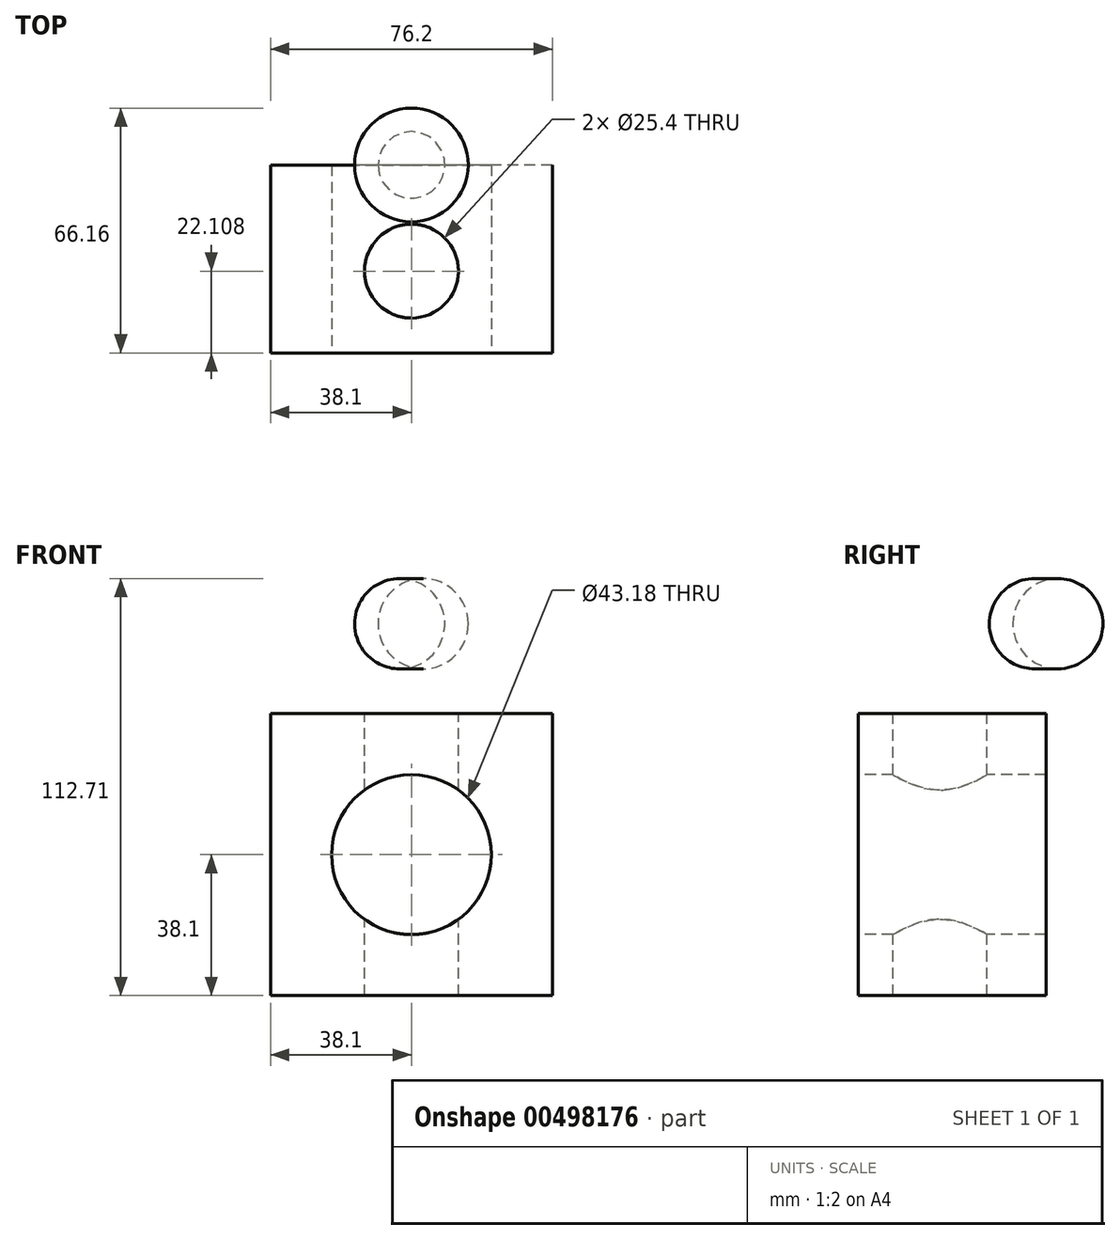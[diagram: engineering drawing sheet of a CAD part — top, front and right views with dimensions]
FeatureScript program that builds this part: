
annotation { "Feature Type Name" : "Feature", "Feature Type Description" : "" }
export const myFeature = defineFeature(function(context is Context, id is Id, definition is map)
    precondition{}
    {
        {
            var Q0;
            Q0=qCreatedBy(makeId("Front.planeOp"),FACE);
            var sketch = newSketch(context, id + "F0", { "sketchPlane" : qUnion([Q0])});
            skLineSegment(sketch, "E0", {"start": v(0, 0) * mm, "end": v(0, -36.26) * mm, "construction": true});
            skSolve(sketch);
        }
        {
            var Q0;
            Q0=qCreatedBy(makeId("Front.planeOp"),FACE);
            var sketch = newSketch(context, id + "F1", { "sketchPlane" : qUnion([Q0])});
            skLineSegment(sketch, "E1.bottom", {"start": v(38.1, 38.1) * mm, "end": v(-38.1, 38.1) * mm});
            skLineSegment(sketch, "E1.top", {"start": v(38.1, -38.1) * mm, "end": v(-38.1, -38.1) * mm});
            skLineSegment(sketch, "E1.left", {"start": v(38.1, 38.1) * mm, "end": v(38.1, -38.1) * mm});
            skLineSegment(sketch, "E1.right", {"start": v(-38.1, 38.1) * mm, "end": v(-38.1, -38.1) * mm});
            skPoint(sketch, "E1.middle", {"position": v(0, 0) * mm});
            skSolve(sketch);
        }
        {
            var Q0;
            Q0 = qSketchRegion(id + "F1", true);
            extrude(context, id + "F2", {"entities" : qUnion([Q0]), "depth" : 50.8 * mm, "offsetDistance" : 25.4 * mm});
        }
        {
            var Q0;
            Q0=makeQuery(id+"F2.opExtrude","SWEPT_FACE",FACE,{"disambiguationData":[OSD([sQuery(id+"F1.wireOp",EDGE,"E1.bottom")])]});
            var sketch = newSketch(context, id + "F3", { "sketchPlane" : qUnion([Q0])});
            skCircle(sketch, "E2", {"center": v(0, -28.7) * mm, "radius": 12.7 * mm});
            skSolve(sketch);
        }
        {
            var Q0;
            Q0 = qSketchRegion(id + "F3", true);
            extrude(context, id + "F4", {"entities" : qUnion([Q0]), "operationType" : NewBodyOperationType.REMOVE, "endBound" : BoundingType.THROUGH_ALL, "oppositeDirection" : true, "depth" : 25.4 * mm, "offsetDistance" : 25.4 * mm});
        }
        {
            var Q0;
            Q0=qCreatedBy(makeId("Front.planeOp"),FACE);
            var sketch = newSketch(context, id + "F5", { "sketchPlane" : qUnion([Q0])});
            skLineSegment(sketch, "E3", {"start": v(0, 50.64) * mm, "end": v(0, 74.2) * mm, "construction": true});
            skArc(sketch, "E4", {"start": v(0, 50.64) * mm, "mid": v(9.03, 62.42) * mm, "end": v(0, 74.2) * mm});
            skLineSegment(sketch, "E5", {"start": v(0, 74.2) * mm, "end": v(0, 50.64) * mm});
            skSolve(sketch);
        }
        {
            var Q0;
            Q0=makeQuery(id+"F5.imprint","IMPRINT",FACE,{"disambiguationData":[TD([[makeQuery(id+"F5.imprint","IMPRINT",EDGE,{"derivedFrom":sQuery(id+"F5.wireOp",EDGE,"E4")}),1.0]])]});
            var Q1;
            Q1=sQuery(id+"F5.wireOp",EDGE,"E5");
            revolve(context, id + "F6", {"entities" : qUnion([Q0]), "axis" : qUnion([Q1]), "revolveType" : RevolveType.FULL});
        }
        {
            var Q0;
            Q0=makeQuery(id+"F2.opExtrude","CAP_FACE",FACE,{"disambiguationData":[OSD([sQuery(id+"F1.wireOp",EDGE,"E1.bottom"),sQuery(id+"F1.wireOp",EDGE,"E1.top"),sQuery(id+"F1.wireOp",EDGE,"E1.left"),sQuery(id+"F1.wireOp",EDGE,"E1.right")])],"isStart":false});
            var sketch = newSketch(context, id + "F7", { "sketchPlane" : qUnion([Q0])});
            skCircle(sketch, "E6", {"center": v(0, 0) * mm, "radius": 21.59 * mm});
            skSolve(sketch);
        }
        {
            var Q0;
            Q0 = qSketchRegion(id + "F7", true);
            extrude(context, id + "F8", {"entities" : qUnion([Q0]), "operationType" : NewBodyOperationType.REMOVE, "endBound" : BoundingType.THROUGH_ALL, "oppositeDirection" : true, "depth" : 25.4 * mm, "offsetDistance" : 25.4 * mm});
        }
    });
